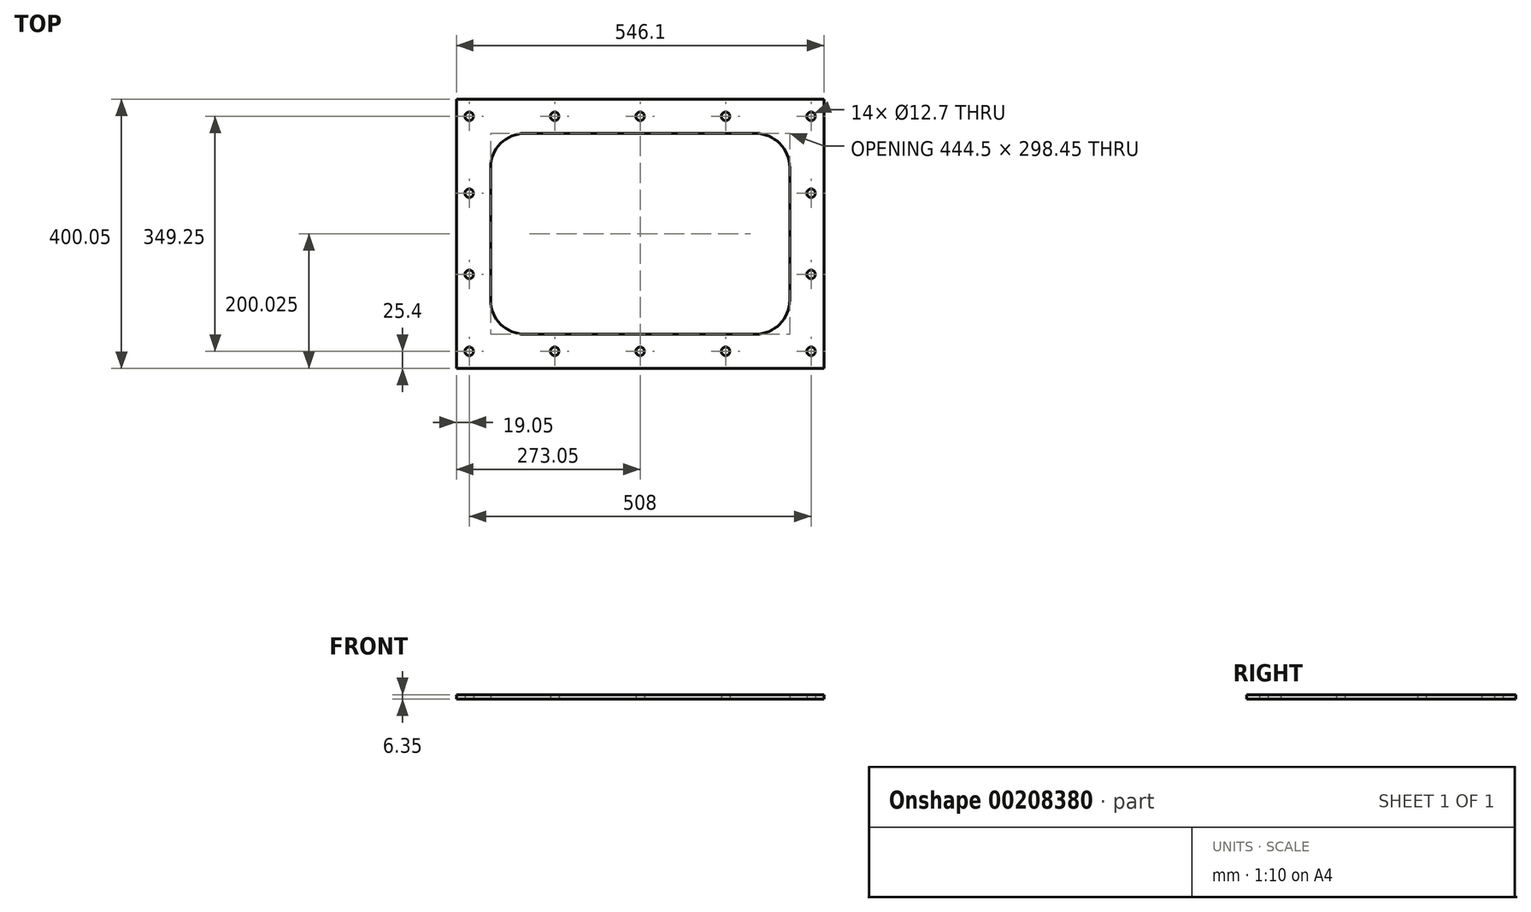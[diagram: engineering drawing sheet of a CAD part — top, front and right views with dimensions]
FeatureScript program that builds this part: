
annotation { "Feature Type Name" : "Feature", "Feature Type Description" : "" }
export const myFeature = defineFeature(function(context is Context, id is Id, definition is map)
    precondition{}
    {
        {
            var Q0;
            Q0=qCreatedBy(makeId("Top.planeOp"),FACE);
            var sketch = newSketch(context, id + "F0", { "sketchPlane" : qUnion([Q0])});
            skLineSegment(sketch, "E0.bottom", {"start": v(0, 0) * mm, "end": v(546.1, 0) * mm});
            skLineSegment(sketch, "E0.top", {"start": v(0, 400.05) * mm, "end": v(546.1, 400.05) * mm});
            skLineSegment(sketch, "E0.left", {"start": v(0, 0) * mm, "end": v(0, 400.05) * mm});
            skLineSegment(sketch, "E0.right", {"start": v(546.1, 0) * mm, "end": v(546.1, 400.05) * mm});
            skLineSegment(sketch, "E1.bottom", {"start": v(101.6, 50.8) * mm, "end": v(444.5, 50.8) * mm});
            skLineSegment(sketch, "E1.top", {"start": v(101.6, 349.25) * mm, "end": v(444.5, 349.25) * mm});
            skLineSegment(sketch, "E1.left", {"start": v(50.8, 101.6) * mm, "end": v(50.8, 298.45) * mm});
            skLineSegment(sketch, "E1.right", {"start": v(495.3, 101.6) * mm, "end": v(495.3, 298.45) * mm});
            skPoint(sketch, "E2.visualSharp", {"position": v(50.8, 349.25) * mm});
            skArc(sketch, "E2.filletArc", {"start": v(101.6, 349.25) * mm, "mid": v(65.68, 334.37) * mm, "end": v(50.8, 298.45) * mm});
            skPoint(sketch, "E3.visualSharp", {"position": v(50.8, 50.8) * mm});
            skArc(sketch, "E3.filletArc", {"start": v(50.8, 101.6) * mm, "mid": v(65.68, 65.68) * mm, "end": v(101.6, 50.8) * mm});
            skPoint(sketch, "E4.visualSharp", {"position": v(495.3, 50.8) * mm});
            skArc(sketch, "E4.filletArc", {"start": v(444.5, 50.8) * mm, "mid": v(480.42, 65.68) * mm, "end": v(495.3, 101.6) * mm});
            skArc(sketch, "E5.filletArc", {"start": v(495.3, 298.45) * mm, "mid": v(480.42, 334.37) * mm, "end": v(444.5, 349.25) * mm});
            skCircle(sketch, "E6", {"center": v(527.05, 374.65) * mm, "radius": 6.35 * mm});
            skCircle(sketch, "E7", {"center": v(527.05, 260.35) * mm, "radius": 6.35 * mm});
            skCircle(sketch, "E8", {"center": v(527.05, 139.7) * mm, "radius": 6.35 * mm});
            skCircle(sketch, "E9", {"center": v(527.05, 25.4) * mm, "radius": 6.35 * mm});
            skLineSegment(sketch, "E10", {"start": v(273.05, 439.08) * mm, "end": v(273.05, -56.66) * mm, "construction": true});
            skPoint(sketch, "E10.startSnap0", {"position": v(273.05, 400.05) * mm});
            skLineSegment(sketch, "E11", {"start": v(-53.69, 200.03) * mm, "end": v(616.44, 200.03) * mm, "construction": true});
            skPoint(sketch, "E11.startSnap0", {"position": v(0, 200.03) * mm});
            skPoint(sketch, "E11.endSnap0", {"position": v(546.1, 200.03) * mm});
            skCircle(sketch, "E12", {"center": v(146.05, 374.65) * mm, "radius": 6.35 * mm});
            skCircle(sketch, "E13", {"center": v(273.05, 374.65) * mm, "radius": 6.35 * mm});
            skCircle(sketch, "E14", {"center": v(400.05, 374.65) * mm, "radius": 6.35 * mm});
            skCircle(sketch, "E15.MirrorC", {"center": v(19.05, 374.65) * mm, "radius": 6.35 * mm});
            skCircle(sketch, "E16.MirrorC", {"center": v(19.05, 260.35) * mm, "radius": 6.35 * mm});
            skCircle(sketch, "E17.MirrorC", {"center": v(19.05, 139.7) * mm, "radius": 6.35 * mm});
            skCircle(sketch, "E18.MirrorC", {"center": v(19.05, 25.4) * mm, "radius": 6.35 * mm});
            skCircle(sketch, "E19.MirrorC", {"center": v(146.05, 25.4) * mm, "radius": 6.35 * mm});
            skCircle(sketch, "E20.MirrorC", {"center": v(273.05, 25.4) * mm, "radius": 6.35 * mm});
            skCircle(sketch, "E21.MirrorC", {"center": v(400.05, 25.4) * mm, "radius": 6.35 * mm});
            skSolve(sketch);
        }
        {
            var Q0;
            Q0=makeQuery(id+"F0.imprint","IMPRINT",FACE,{"disambiguationData":[TD([[makeQuery(id+"F0.imprint","IMPRINT",EDGE,{"derivedFrom":sQuery(id+"F0.wireOp",EDGE,"E0.bottom")}),1.0]])]});
            extrude(context, id + "F1", {"entities" : qUnion([Q0]), "depth" : 3.17 * mm});
        }
        {
            var Q0;
            Q0 = qSketchRegion(id + "F0", true);
            var Q1;
            Q1=makeQuery(id+"F1.opExtrude","CAP_FACE",FACE,{"disambiguationData":[OSD([sQuery(id+"F0.wireOp",EDGE,"E0.bottom"),sQuery(id+"F0.wireOp",EDGE,"E0.top"),sQuery(id+"F0.wireOp",EDGE,"E0.left"),sQuery(id+"F0.wireOp",EDGE,"E0.right"),sQuery(id+"F0.wireOp",EDGE,"E1.bottom"),sQuery(id+"F0.wireOp",EDGE,"E1.top"),sQuery(id+"F0.wireOp",EDGE,"E1.left"),sQuery(id+"F0.wireOp",EDGE,"E1.right"),sQuery(id+"F0.wireOp",EDGE,"E2.filletArc"),sQuery(id+"F0.wireOp",EDGE,"E3.filletArc"),sQuery(id+"F0.wireOp",EDGE,"E4.filletArc"),sQuery(id+"F0.wireOp",EDGE,"E5.filletArc"),sQuery(id+"F0.wireOp",EDGE,"E6"),sQuery(id+"F0.wireOp",EDGE,"E7"),sQuery(id+"F0.wireOp",EDGE,"E8"),sQuery(id+"F0.wireOp",EDGE,"E9"),sQuery(id+"F0.wireOp",EDGE,"E12"),sQuery(id+"F0.wireOp",EDGE,"E13"),sQuery(id+"F0.wireOp",EDGE,"E14"),sQuery(id+"F0.wireOp",EDGE,"E15.MirrorC"),sQuery(id+"F0.wireOp",EDGE,"E16.MirrorC"),sQuery(id+"F0.wireOp",EDGE,"E17.MirrorC"),sQuery(id+"F0.wireOp",EDGE,"E18.MirrorC"),sQuery(id+"F0.wireOp",EDGE,"E19.MirrorC"),sQuery(id+"F0.wireOp",EDGE,"E20.MirrorC"),sQuery(id+"F0.wireOp",EDGE,"E21.MirrorC")])],"isStart":false});
            extrude(context, id + "F2", {"entities" : qUnion([Q0, Q1]), "operationType" : NewBodyOperationType.ADD, "depth" : 3.17 * mm});
        }
    });
